# Revit family: CADS_Vent-Axia_MechEquip_Fan_LCA_1000_3Ph4P - SUPPLY
name_source: partatom
category: Mechanical Equipment
units: mm (PartAtom-declared; Revit-internal decimal feet)

## family parameters
Always vertical = Yes
Cut with Voids When Loaded = No
OmniClass Number = 23.75.00.00
OmniClass Title = Climate Control (HVAC)
Part Type = Normal
Room Calculation Point = No
Round Connector Dimension = Use Diameter
Shared = No
Work Plane-Based = No

## types (15) — shared parameters
AirflowRateRange = 0.0 L/s
AssemblyPlace = UNKNOWN
AssetType = FIXED
DurationUnit = Year
ExteriorInsulation = No
Fitting Type = Ignore
GrossWeight = 0.00 kg
HasProtectiveEarth = No
IfcExportAs = IfcFanType
IsExtendedWarranty = No
ManufacturerAddress = Fleming Way
Crawley 
RH10 9YX
NominalDiameter = 1000 mm  [stored 3.28084 ft]
NominalHeight = 1000 mm  [stored 3.28084 ft]
NominalWidth = 1000 mm  [stored 3.28084 ft]
Quantity = 1
RatedCurrent = 0 A
RatedVoltage = 0 V
Status = New
WarrantyGuarantor = Vent-Axia Limited
WorkingPressure = 0.0 Pa
nr = 500 mm  [stored 1.64042 ft]
zero-valued in all types: CADS_Index, CADS_Usage, Default Elevation, ExpectedServiceLife, NumberOfPoles

## per-type parameters (varying)
| type | ModelReference | NominalLength |
| LCA1003410 | LCAX 1000mm 3PH 4P 10DEG | 565 mm  [stored 1.85367 ft] |
| LCA1003412 | LCAX 1000mm 3PH 4P 12DEG | 565 mm  [stored 1.85367 ft] |
| LCA1003414 | LCAX 1000mm 3PH 4P 14DEG | 565 mm  [stored 1.85367 ft] |
| LCA1003416 | LCAX 1000mm 3PH 4P 16DEG | 565 mm  [stored 1.85367 ft] |
| LCA1003418 | LCAX 1000mm 3PH 4P 18DEG | 565 mm  [stored 1.85367 ft] |
| LCA1003420 | LCAX 1000mm 3PH 4P 20DEG | 565 mm  [stored 1.85367 ft] |
| LCA1003422 | LCAX 1000mm 3PH 4P 22DEG | 565 mm  [stored 1.85367 ft] |
| LCA1003424 | LCAX 1000mm 3PH 4P 24DEG | 700 mm  [stored 2.29659 ft] |
| LCA1003426 | LCAX 1000mm 3PH 4P 26DEG | 700 mm  [stored 2.29659 ft] |
| LCA1003428 | LCAX 1000mm 3PH 4P 28DEG | 700 mm  [stored 2.29659 ft] |
| LCA1003430 | LCAX 1000mm 3PH 4P 30DEG | 700 mm  [stored 2.29659 ft] |
| LCA1003434 | LCAX 1000mm 3PH 4P 34DEG | 790 mm  [stored 2.59186 ft] |
| LCA1003436 | LCAX 1000mm 3PH 4P 36DEG | 790 mm  [stored 2.59186 ft] |
| LCA1003438 | LCAX 1000mm 3PH 4P 38DEG | 790 mm  [stored 2.59186 ft] |
| LCA1003440 | LCAX 1000mm 3PH 4P 40DEG | 790 mm  [stored 2.59186 ft] |

note: column(s) folded — value = type name in every type: ModelNumber

note: [stored X ft] marks values corroborated as IEEE doubles in the binary element streams (Revit-internal decimal feet)

## geometry (parser evidence)
native form markers: Sweep x11
no freeform markers — native parametric forms only
